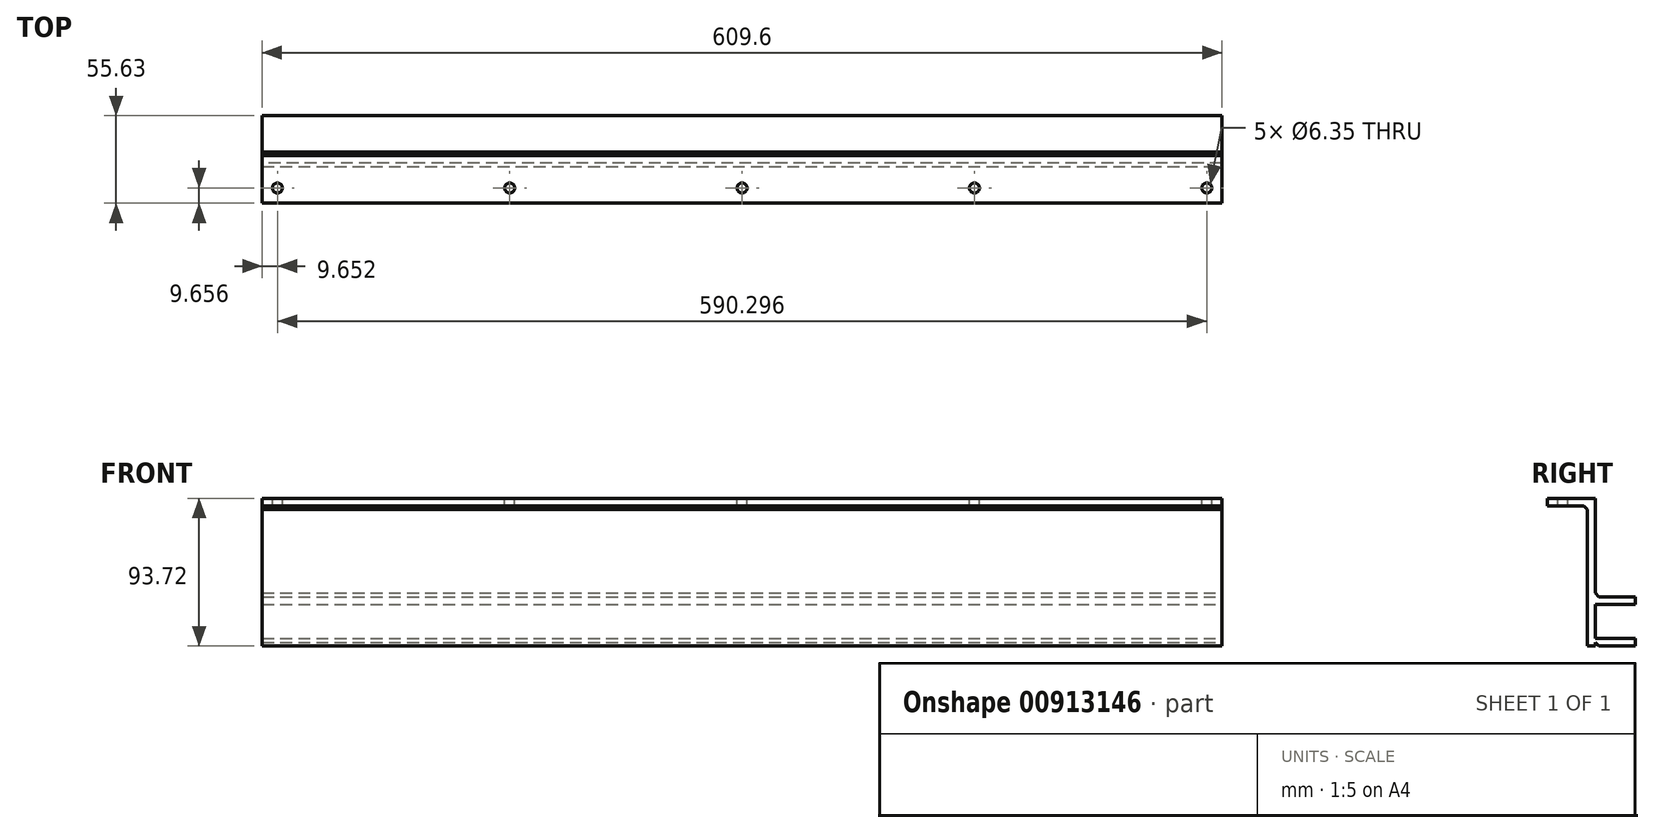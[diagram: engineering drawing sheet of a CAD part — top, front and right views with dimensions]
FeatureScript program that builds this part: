
annotation { "Feature Type Name" : "Feature", "Feature Type Description" : "" }
export const myFeature = defineFeature(function(context is Context, id is Id, definition is map)
    precondition{}
    {
        {
            var Q0;
            Q0=qCreatedBy(makeId("Front.planeOp"),FACE);
            var sketch = newSketch(context, id + "F0", { "sketchPlane" : qUnion([Q0])});
            skLineSegment(sketch, "E0.bottom", {"start": v(304.8, -46.86) * mm, "end": v(-304.8, -46.86) * mm});
            skLineSegment(sketch, "E0.top", {"start": v(304.8, 46.86) * mm, "end": v(-304.8, 46.86) * mm});
            skLineSegment(sketch, "E0.left", {"start": v(304.8, -46.86) * mm, "end": v(304.8, 46.86) * mm});
            skLineSegment(sketch, "E0.right", {"start": v(-304.8, -46.86) * mm, "end": v(-304.8, 46.86) * mm});
            skPoint(sketch, "E0.middle", {"position": v(0, 0) * mm});
            skSolve(sketch);
        }
        {
            var Q0;
            Q0 = qSketchRegion(id + "F0", true);
            extrude(context, id + "F1", {"entities" : qUnion([Q0]), "depth" : 4.83 * mm, "offsetDistance" : 25.4 * mm});
        }
        {
            var Q0;
            Q0=makeQuery(id+"F1.opExtrude","SWEPT_FACE",FACE,{"disambiguationData":[OSD([sQuery(id+"F0.wireOp",EDGE,"E0.left")])]});
            var sketch = newSketch(context, id + "F2", { "sketchPlane" : qUnion([Q0])});
            skLineSegment(sketch, "E1.bottom", {"start": v(0, -46.86) * mm, "end": v(25.4, -46.86) * mm});
            skLineSegment(sketch, "E1.top", {"start": v(0, -42.04) * mm, "end": v(25.4, -42.04) * mm});
            skLineSegment(sketch, "E1.left", {"start": v(0, -46.86) * mm, "end": v(0, -42.04) * mm});
            skLineSegment(sketch, "E1.right", {"start": v(25.4, -46.86) * mm, "end": v(25.4, -42.04) * mm});
            skLineSegment(sketch, "E2.bottom", {"start": v(-30.23, 46.86) * mm, "end": v(0, 46.86) * mm});
            skLineSegment(sketch, "E2.top", {"start": v(-30.23, 42.04) * mm, "end": v(0, 42.04) * mm});
            skLineSegment(sketch, "E2.left", {"start": v(0, 46.86) * mm, "end": v(0, 42.04) * mm});
            skLineSegment(sketch, "E2.right", {"start": v(-30.23, 46.86) * mm, "end": v(-30.23, 42.04) * mm});
            skLineSegment(sketch, "E3.bottom", {"start": v(0, -20.45) * mm, "end": v(25.4, -20.45) * mm});
            skLineSegment(sketch, "E3.top", {"start": v(0, -15.62) * mm, "end": v(25.4, -15.62) * mm});
            skLineSegment(sketch, "E3.left", {"start": v(0, -20.45) * mm, "end": v(0, -15.62) * mm});
            skLineSegment(sketch, "E3.right", {"start": v(25.4, -20.45) * mm, "end": v(25.4, -15.62) * mm});
            skLineSegment(sketch, "E4", {"start": v(2.29, -15.62) * mm, "end": v(0, -13.33) * mm});
            skLineSegment(sketch, "E5", {"start": v(2.29, -46.86) * mm, "end": v(0, -44.58) * mm});
            skLineSegment(sketch, "E6", {"start": v(-7.11, 42.04) * mm, "end": v(-4.83, 39.75) * mm});
            skSolve(sketch);
        }
        {
            var Q0;
            {var subQ3=sQuery(id+"F2.wireOp",EDGE,"E4");Q0=makeQuery(id+"F2.imprint","IMPRINT",FACE,{"disambiguationData":[TD([[makeQuery(id+"F2.imprint","IMPRINT",EDGE,{"derivedFrom":subQ3}),1.0]])]});}
            var Q1;
            Q1=makeQuery(id+"F2.imprint","IMPRINT",FACE,{"disambiguationData":[TD([[makeQuery(id+"F2.imprint","IMPRINT",EDGE,{"derivedFrom":sQuery(id+"F2.wireOp",EDGE,"E3.bottom")}),1.0]])]});
            var Q2;
            Q2=makeQuery(id+"F2.imprint","IMPRINT",FACE,{"disambiguationData":[TD([[makeQuery(id+"F2.imprint","IMPRINT",EDGE,{"derivedFrom":sQuery(id+"F2.wireOp",EDGE,"E2.bottom")}),-1.0]])]});
            var Q3;
            {var subQ2=sQuery(id+"F2.wireOp",EDGE,"E1.top");Q3=makeQuery(id+"F2.imprint","IMPRINT",FACE,{"disambiguationData":[TD([[makeQuery(id+"F2.imprint","IMPRINT",EDGE,{"derivedFrom":subQ2}),-1.0]])]});}
            var Q4;
            {var subQ0=sQuery(id+"F2.wireOp",EDGE,"E2.right");Q4=makeQuery(id+"F2.imprint","IMPRINT",FACE,{"disambiguationData":[TD([[makeQuery(id+"F2.imprint","IMPRINT",EDGE,{"derivedFrom":subQ0}),1.0]])]});}
            var Q5;
            {var subQ0=sQuery(id+"F2.wireOp",EDGE,"E6");Q5=makeQuery(id+"F2.imprint","IMPRINT",FACE,{"disambiguationData":[TD([[makeQuery(id+"F2.imprint","IMPRINT",EDGE,{"derivedFrom":subQ0}),1.0]])]});}
            var Q6;
            Q6=makeQuery(id+"F1.opExtrude","SWEPT_FACE",FACE,{"disambiguationData":[OSD([sQuery(id+"F0.wireOp",EDGE,"E0.right")])]});
            extrude(context, id + "F3", {"entities" : qUnion([Q0, Q1, Q2, Q3, Q4, Q5]), "operationType" : NewBodyOperationType.ADD, "endBound" : BoundingType.UP_TO_SURFACE, "oppositeDirection" : true, "depth" : 25.4 * mm, "endBoundEntityFace" : qUnion([Q6]), "offsetDistance" : 25.4 * mm});
        }
        {
            var Q0;
            Q0=makeQuery(id+"F3.boolean.opBoolean","MERGE",FACE,{"derivedFrom":[makeQuery(id+"F1.opExtrude","SWEPT_FACE",FACE,{"disambiguationData":[OSD([sQuery(id+"F0.wireOp",EDGE,"E0.top")])]}),makeQuery(id+"F3.opExtrude","SWEPT_FACE",FACE,{"disambiguationData":[OSD([sQuery(id+"F2.wireOp",EDGE,"E2.bottom")])]})]});
            var sketch = newSketch(context, id + "F4", { "sketchPlane" : qUnion([Q0])});
            skPoint(sketch, "E7", {"position": v(-295.15, -20.57) * mm});
            skPoint(sketch, "E8", {"position": v(-147.57, -20.57) * mm});
            skPoint(sketch, "E9", {"position": v(0, -20.57) * mm});
            skPoint(sketch, "E10", {"position": v(147.57, -20.57) * mm});
            skPoint(sketch, "E11", {"position": v(295.15, -20.57) * mm});
            skSolve(sketch);
        }
        {
            var Q0;
            Q0=sQuery(id+"F4.wireOp",VERTEX,"E7");
            var Q1;
            Q1=sQuery(id+"F4.wireOp",VERTEX,"E8");
            var Q2;
            Q2=sQuery(id+"F4.wireOp",VERTEX,"E9");
            var Q3;
            Q3=sQuery(id+"F4.wireOp",VERTEX,"E10");
            var Q4;
            Q4=sQuery(id+"F4.wireOp",VERTEX,"E11");
            var Q5;
            Q5=makeQuery(id+"F1.opExtrude","SWEPT_BODY",BODY,{"disambiguationData":[OSD([sQuery(id+"F0.wireOp",EDGE,"E0.bottom"),sQuery(id+"F0.wireOp",EDGE,"E0.top"),sQuery(id+"F0.wireOp",EDGE,"E0.left"),sQuery(id+"F0.wireOp",EDGE,"E0.right")])]});
            hole(context, id + "F5", {"style" : HoleStyle.SIMPLE, "endStyle" : HoleEndStyle.THROUGH, "holeDiameter" : 6.35 * mm, "majorDiameter" : 6.35 * mm, "isTappedThrough" : true, "tappedDepth" : 12.7 * mm, "tapClearance" : 3, "locations" : qUnion([Q0, Q1, Q2, Q3, Q4]), "scope" : qUnion([Q5])});
        }
    });
